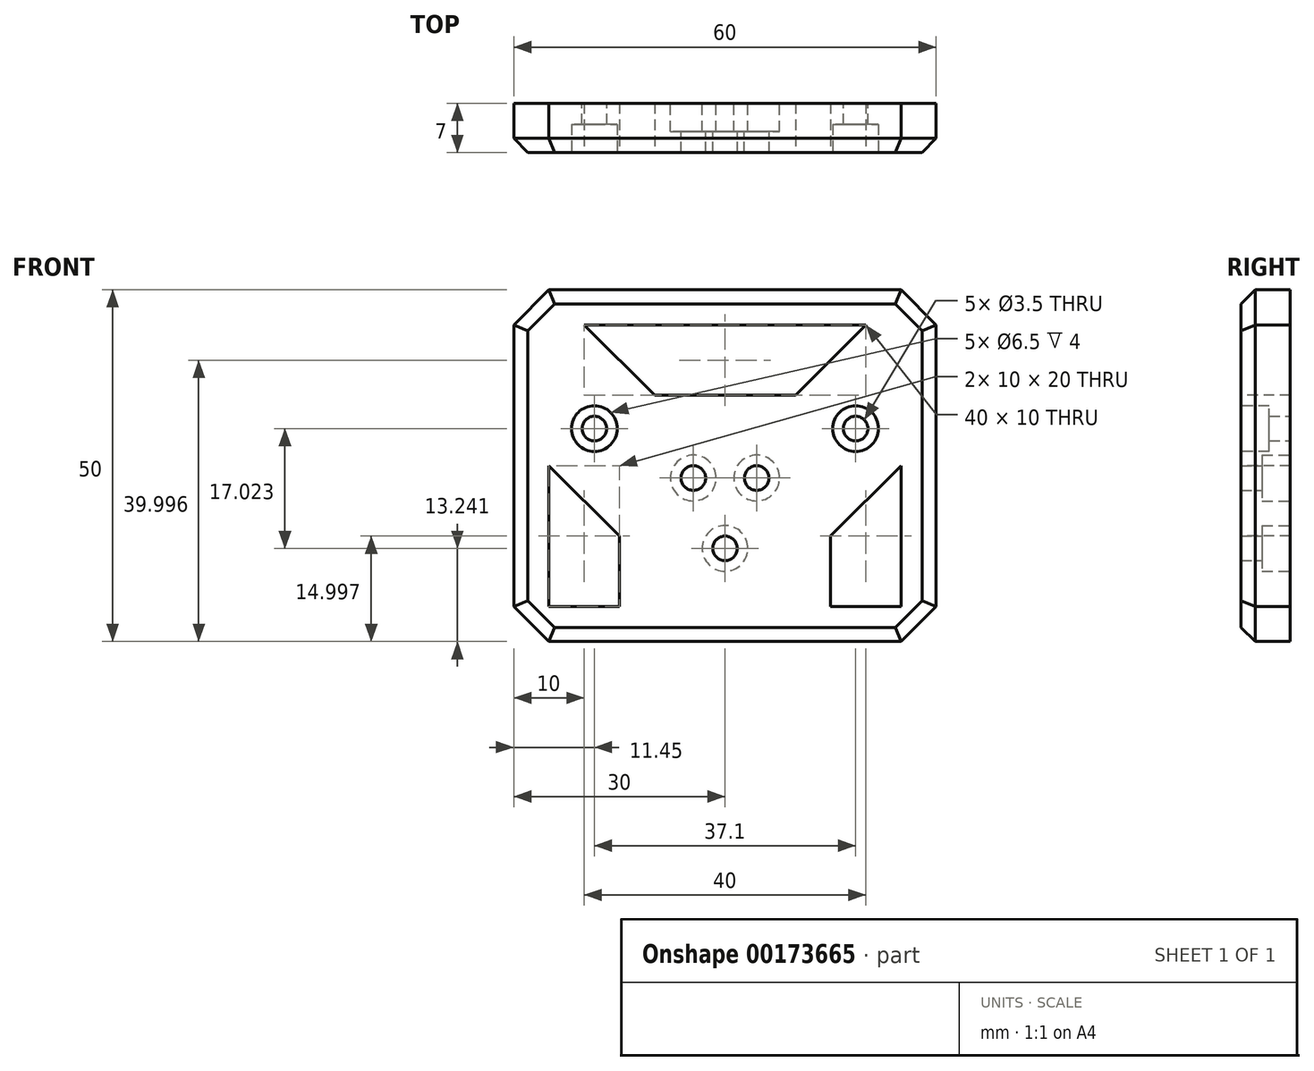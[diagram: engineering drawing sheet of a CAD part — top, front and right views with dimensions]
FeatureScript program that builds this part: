
annotation { "Feature Type Name" : "Feature", "Feature Type Description" : "" }
export const myFeature = defineFeature(function(context is Context, id is Id, definition is map)
    precondition{}
    {
        {
            var Q0;
            Q0=qCreatedBy(makeId("Front.planeOp"),FACE);
            var sketch = newSketch(context, id + "F0", { "sketchPlane" : qUnion([Q0])});
            skLineSegment(sketch, "E0", {"start": v(-30, 0) * mm, "end": v(30, 0) * mm, "construction": true});
            skLineSegment(sketch, "E1", {"start": v(30, 41.75) * mm, "end": v(-30, 41.75) * mm});
            skLineSegment(sketch, "E2", {"start": v(-30, 41.75) * mm, "end": v(-30, -8.25) * mm});
            skLineSegment(sketch, "E3", {"start": v(-30, -8.25) * mm, "end": v(30, -8.25) * mm});
            skLineSegment(sketch, "E4", {"start": v(30, -8.25) * mm, "end": v(30, 41.75) * mm});
            skLineSegment(sketch, "E5", {"start": v(-18.55, 22.01) * mm, "end": v(18.55, 22.01) * mm, "construction": true});
            skPoint(sketch, "E6", {"position": v(0, 22.01) * mm});
            skCircle(sketch, "E7", {"center": v(-18.55, 22.01) * mm, "radius": 1.75 * mm});
            skCircle(sketch, "E8", {"center": v(18.55, 22.01) * mm, "radius": 1.75 * mm});
            skPoint(sketch, "E9", {"position": v(0, 15) * mm});
            skLineSegment(sketch, "E10", {"start": v(-4.5, 15) * mm, "end": v(4.5, 15) * mm, "construction": true});
            skLineSegment(sketch, "E11", {"start": v(0, 15) * mm, "end": v(0, 5) * mm, "construction": true});
            skCircle(sketch, "E12", {"center": v(-4.5, 15) * mm, "radius": 1.75 * mm});
            skCircle(sketch, "E13", {"center": v(4.5, 15) * mm, "radius": 1.75 * mm});
            skCircle(sketch, "E14", {"center": v(0, 5) * mm, "radius": 1.75 * mm});
            skSolve(sketch);
        }
        {
            var Q0;
            Q0 = qSketchRegion(id + "F0", true);
            extrude(context, id + "F1", {"entities" : qUnion([Q0]), "depth" : 7 * mm});
        }
        {
            var Q0;
            Q0=makeQuery(id+"F1.opExtrude","SWEPT_EDGE",EDGE,{"disambiguationData":[OSD([sQuery(id+"F0.wireOp",EDGE,"E2"),sQuery(id+"F0.wireOp",EDGE,"E3")])]});
            var Q1;
            Q1=makeQuery(id+"F1.opExtrude","SWEPT_EDGE",EDGE,{"disambiguationData":[OSD([sQuery(id+"F0.wireOp",EDGE,"E3"),sQuery(id+"F0.wireOp",EDGE,"E4")])]});
            var Q2;
            Q2=makeQuery(id+"F1.opExtrude","SWEPT_EDGE",EDGE,{"disambiguationData":[OSD([sQuery(id+"F0.wireOp",EDGE,"E1"),sQuery(id+"F0.wireOp",EDGE,"E4")])]});
            var Q3;
            Q3=makeQuery(id+"F1.opExtrude","SWEPT_EDGE",EDGE,{"disambiguationData":[OSD([sQuery(id+"F0.wireOp",EDGE,"E1"),sQuery(id+"F0.wireOp",EDGE,"E2")])]});
            chamfer(context, id + "F2", {"entities" : qUnion([Q0, Q1, Q2, Q3]), "width" : 5 * mm, "tangentPropagation" : true});
        }
        {
            var Q0;
            Q0=makeQuery(id+"F1.opExtrude","CAP_FACE",FACE,{"disambiguationData":[OSD([sQuery(id+"F0.wireOp",EDGE,"E1"),sQuery(id+"F0.wireOp",EDGE,"E2"),sQuery(id+"F0.wireOp",EDGE,"E3"),sQuery(id+"F0.wireOp",EDGE,"E4"),sQuery(id+"F0.wireOp",EDGE,"E7"),sQuery(id+"F0.wireOp",EDGE,"E8"),sQuery(id+"F0.wireOp",EDGE,"E12"),sQuery(id+"F0.wireOp",EDGE,"E13"),sQuery(id+"F0.wireOp",EDGE,"E14")])],"isStart":true});
            var sketch = newSketch(context, id + "F3", { "sketchPlane" : qUnion([Q0])});
            skCircle(sketch, "E15", {"center": v(-4.5, 15) * mm, "radius": 3.25 * mm});
            skCircle(sketch, "E16", {"center": v(4.5, 15) * mm, "radius": 3.25 * mm});
            skCircle(sketch, "E17", {"center": v(0, 5) * mm, "radius": 3.25 * mm});
            skSolve(sketch);
        }
        {
            var Q0;
            Q0 = qSketchRegion(id + "F3", true);
            extrude(context, id + "F4", {"entities" : qUnion([Q0]), "operationType" : NewBodyOperationType.REMOVE, "oppositeDirection" : true, "depth" : 4 * mm});
        }
        {
            var Q0;
            Q0=makeQuery(id+"F1.opExtrude","CAP_FACE",FACE,{"disambiguationData":[OSD([sQuery(id+"F0.wireOp",EDGE,"E1"),sQuery(id+"F0.wireOp",EDGE,"E2"),sQuery(id+"F0.wireOp",EDGE,"E3"),sQuery(id+"F0.wireOp",EDGE,"E4"),sQuery(id+"F0.wireOp",EDGE,"E7"),sQuery(id+"F0.wireOp",EDGE,"E8"),sQuery(id+"F0.wireOp",EDGE,"E12"),sQuery(id+"F0.wireOp",EDGE,"E13"),sQuery(id+"F0.wireOp",EDGE,"E14")])],"isStart":false});
            var sketch = newSketch(context, id + "F5", { "sketchPlane" : qUnion([Q0])});
            skCircle(sketch, "E18", {"center": v(-18.55, 22.01) * mm, "radius": 3.25 * mm});
            skCircle(sketch, "E19", {"center": v(18.55, 22.01) * mm, "radius": 3.25 * mm});
            skSolve(sketch);
        }
        {
            var Q0;
            Q0 = qSketchRegion(id + "F5", true);
            extrude(context, id + "F6", {"entities" : qUnion([Q0]), "operationType" : NewBodyOperationType.REMOVE, "oppositeDirection" : true, "depth" : 4 * mm});
        }
        {
            var Q0;
            Q0=makeQuery(id+"F1.opExtrude","CAP_FACE",FACE,{"disambiguationData":[OSD([sQuery(id+"F0.wireOp",EDGE,"E1"),sQuery(id+"F0.wireOp",EDGE,"E2"),sQuery(id+"F0.wireOp",EDGE,"E3"),sQuery(id+"F0.wireOp",EDGE,"E4"),sQuery(id+"F0.wireOp",EDGE,"E7"),sQuery(id+"F0.wireOp",EDGE,"E8"),sQuery(id+"F0.wireOp",EDGE,"E12"),sQuery(id+"F0.wireOp",EDGE,"E13"),sQuery(id+"F0.wireOp",EDGE,"E14")])],"isStart":false});
            var sketch = newSketch(context, id + "F7", { "sketchPlane" : qUnion([Q0])});
            skLineSegment(sketch, "E20", {"start": v(0, 36.75) * mm, "end": v(-20, 36.75) * mm});
            skLineSegment(sketch, "E21", {"start": v(-20, 36.75) * mm, "end": v(-10, 26.75) * mm});
            skLineSegment(sketch, "E22", {"start": v(-10, 26.75) * mm, "end": v(0, 26.75) * mm});
            skLineSegment(sketch, "E23", {"start": v(0, 26.75) * mm, "end": v(10, 26.75) * mm});
            skPoint(sketch, "E23.endSnap0", {"position": v(-5, 26.75) * mm});
            skLineSegment(sketch, "E24", {"start": v(10, 26.75) * mm, "end": v(20, 36.75) * mm});
            skLineSegment(sketch, "E25", {"start": v(20, 36.75) * mm, "end": v(0, 36.75) * mm});
            skLineSegment(sketch, "E26", {"start": v(25, 16.75) * mm, "end": v(25, -3.25) * mm});
            skLineSegment(sketch, "E27", {"start": v(25, -3.25) * mm, "end": v(15, -3.25) * mm});
            skLineSegment(sketch, "E28", {"start": v(15, -3.25) * mm, "end": v(15, 6.75) * mm});
            skLineSegment(sketch, "E29", {"start": v(15, 6.75) * mm, "end": v(25, 16.75) * mm});
            skLineSegment(sketch, "E30", {"start": v(-25, 16.75) * mm, "end": v(-25, -3.25) * mm});
            skLineSegment(sketch, "E31", {"start": v(-25, -3.25) * mm, "end": v(-15, -3.25) * mm});
            skLineSegment(sketch, "E32", {"start": v(-15, -3.25) * mm, "end": v(-15, 6.75) * mm});
            skLineSegment(sketch, "E33", {"start": v(-15, 6.75) * mm, "end": v(-25, 16.75) * mm});
            skSolve(sketch);
        }
        {
            var Q0;
            Q0 = qSketchRegion(id + "F7", true);
            extrude(context, id + "F8", {"entities" : qUnion([Q0]), "operationType" : NewBodyOperationType.REMOVE, "endBound" : BoundingType.THROUGH_ALL, "oppositeDirection" : true, "depth" : 25 * mm});
        }
        {
            var Q0;
            Q0=makeQuery(id+"F1.opExtrude","CAP_EDGE",EDGE,{"disambiguationData":[OSD([sQuery(id+"F0.wireOp",EDGE,"E1")])],"isStart":false});
            var Q1;
            {var subQ0=sQuery(id+"F0.wireOp",EDGE,"E4");var subQ1=sQuery(id+"F0.wireOp",EDGE,"E1");Q1=makeQuery(id+"F2.opChamfer","BLEND_EDGE",EDGE,{"blendedFrom":[makeQuery(id+"F1.opExtrude","SWEPT_EDGE",EDGE,{"disambiguationData":[OSD([subQ1,subQ0])]}),makeQuery(id+"F1.opExtrude","CAP_FACE",FACE,{"disambiguationData":[OSD([subQ1,sQuery(id+"F0.wireOp",EDGE,"E2"),sQuery(id+"F0.wireOp",EDGE,"E3"),subQ0,sQuery(id+"F0.wireOp",EDGE,"E7"),sQuery(id+"F0.wireOp",EDGE,"E8"),sQuery(id+"F0.wireOp",EDGE,"E12"),sQuery(id+"F0.wireOp",EDGE,"E13"),sQuery(id+"F0.wireOp",EDGE,"E14")])],"isStart":false})],"blendedInto":[makeQuery(id+"F1.opExtrude","CAP_FACE",FACE,{"disambiguationData":[OSD([subQ1,sQuery(id+"F0.wireOp",EDGE,"E2"),sQuery(id+"F0.wireOp",EDGE,"E3"),subQ0,sQuery(id+"F0.wireOp",EDGE,"E7"),sQuery(id+"F0.wireOp",EDGE,"E8"),sQuery(id+"F0.wireOp",EDGE,"E12"),sQuery(id+"F0.wireOp",EDGE,"E13"),sQuery(id+"F0.wireOp",EDGE,"E14")])],"isStart":false})]});}
            var Q2;
            {var subQ0=sQuery(id+"F0.wireOp",EDGE,"E2");var subQ1=sQuery(id+"F0.wireOp",EDGE,"E1");Q2=makeQuery(id+"F2.opChamfer","BLEND_EDGE",EDGE,{"blendedFrom":[makeQuery(id+"F1.opExtrude","SWEPT_EDGE",EDGE,{"disambiguationData":[OSD([subQ1,subQ0])]}),makeQuery(id+"F1.opExtrude","CAP_FACE",FACE,{"disambiguationData":[OSD([subQ1,subQ0,sQuery(id+"F0.wireOp",EDGE,"E3"),sQuery(id+"F0.wireOp",EDGE,"E4"),sQuery(id+"F0.wireOp",EDGE,"E7"),sQuery(id+"F0.wireOp",EDGE,"E8"),sQuery(id+"F0.wireOp",EDGE,"E12"),sQuery(id+"F0.wireOp",EDGE,"E13"),sQuery(id+"F0.wireOp",EDGE,"E14")])],"isStart":false})],"blendedInto":[makeQuery(id+"F1.opExtrude","CAP_FACE",FACE,{"disambiguationData":[OSD([subQ1,subQ0,sQuery(id+"F0.wireOp",EDGE,"E3"),sQuery(id+"F0.wireOp",EDGE,"E4"),sQuery(id+"F0.wireOp",EDGE,"E7"),sQuery(id+"F0.wireOp",EDGE,"E8"),sQuery(id+"F0.wireOp",EDGE,"E12"),sQuery(id+"F0.wireOp",EDGE,"E13"),sQuery(id+"F0.wireOp",EDGE,"E14")])],"isStart":false})]});}
            var Q3;
            Q3=makeQuery(id+"F1.opExtrude","CAP_EDGE",EDGE,{"disambiguationData":[OSD([sQuery(id+"F0.wireOp",EDGE,"E4")])],"isStart":false});
            var Q4;
            {var subQ0=sQuery(id+"F0.wireOp",EDGE,"E4");var subQ1=sQuery(id+"F0.wireOp",EDGE,"E3");Q4=makeQuery(id+"F2.opChamfer","BLEND_EDGE",EDGE,{"blendedFrom":[makeQuery(id+"F1.opExtrude","SWEPT_EDGE",EDGE,{"disambiguationData":[OSD([subQ1,subQ0])]}),makeQuery(id+"F1.opExtrude","CAP_FACE",FACE,{"disambiguationData":[OSD([sQuery(id+"F0.wireOp",EDGE,"E1"),sQuery(id+"F0.wireOp",EDGE,"E2"),subQ1,subQ0,sQuery(id+"F0.wireOp",EDGE,"E7"),sQuery(id+"F0.wireOp",EDGE,"E8"),sQuery(id+"F0.wireOp",EDGE,"E12"),sQuery(id+"F0.wireOp",EDGE,"E13"),sQuery(id+"F0.wireOp",EDGE,"E14")])],"isStart":false})],"blendedInto":[makeQuery(id+"F1.opExtrude","CAP_FACE",FACE,{"disambiguationData":[OSD([sQuery(id+"F0.wireOp",EDGE,"E1"),sQuery(id+"F0.wireOp",EDGE,"E2"),subQ1,subQ0,sQuery(id+"F0.wireOp",EDGE,"E7"),sQuery(id+"F0.wireOp",EDGE,"E8"),sQuery(id+"F0.wireOp",EDGE,"E12"),sQuery(id+"F0.wireOp",EDGE,"E13"),sQuery(id+"F0.wireOp",EDGE,"E14")])],"isStart":false})]});}
            var Q5;
            Q5=makeQuery(id+"F1.opExtrude","CAP_EDGE",EDGE,{"disambiguationData":[OSD([sQuery(id+"F0.wireOp",EDGE,"E3")])],"isStart":false});
            var Q6;
            {var subQ0=sQuery(id+"F0.wireOp",EDGE,"E3");var subQ1=sQuery(id+"F0.wireOp",EDGE,"E2");Q6=makeQuery(id+"F2.opChamfer","BLEND_EDGE",EDGE,{"blendedFrom":[makeQuery(id+"F1.opExtrude","SWEPT_EDGE",EDGE,{"disambiguationData":[OSD([subQ1,subQ0])]}),makeQuery(id+"F1.opExtrude","CAP_FACE",FACE,{"disambiguationData":[OSD([sQuery(id+"F0.wireOp",EDGE,"E1"),subQ1,subQ0,sQuery(id+"F0.wireOp",EDGE,"E4"),sQuery(id+"F0.wireOp",EDGE,"E7"),sQuery(id+"F0.wireOp",EDGE,"E8"),sQuery(id+"F0.wireOp",EDGE,"E12"),sQuery(id+"F0.wireOp",EDGE,"E13"),sQuery(id+"F0.wireOp",EDGE,"E14")])],"isStart":false})],"blendedInto":[makeQuery(id+"F1.opExtrude","CAP_FACE",FACE,{"disambiguationData":[OSD([sQuery(id+"F0.wireOp",EDGE,"E1"),subQ1,subQ0,sQuery(id+"F0.wireOp",EDGE,"E4"),sQuery(id+"F0.wireOp",EDGE,"E7"),sQuery(id+"F0.wireOp",EDGE,"E8"),sQuery(id+"F0.wireOp",EDGE,"E12"),sQuery(id+"F0.wireOp",EDGE,"E13"),sQuery(id+"F0.wireOp",EDGE,"E14")])],"isStart":false})]});}
            var Q7;
            Q7=makeQuery(id+"F1.opExtrude","CAP_EDGE",EDGE,{"disambiguationData":[OSD([sQuery(id+"F0.wireOp",EDGE,"E2")])],"isStart":false});
            chamfer(context, id + "F9", {"entities" : qUnion([Q0, Q1, Q2, Q3, Q4, Q5, Q6, Q7]), "width" : 2 * mm, "tangentPropagation" : true});
        }
    });
